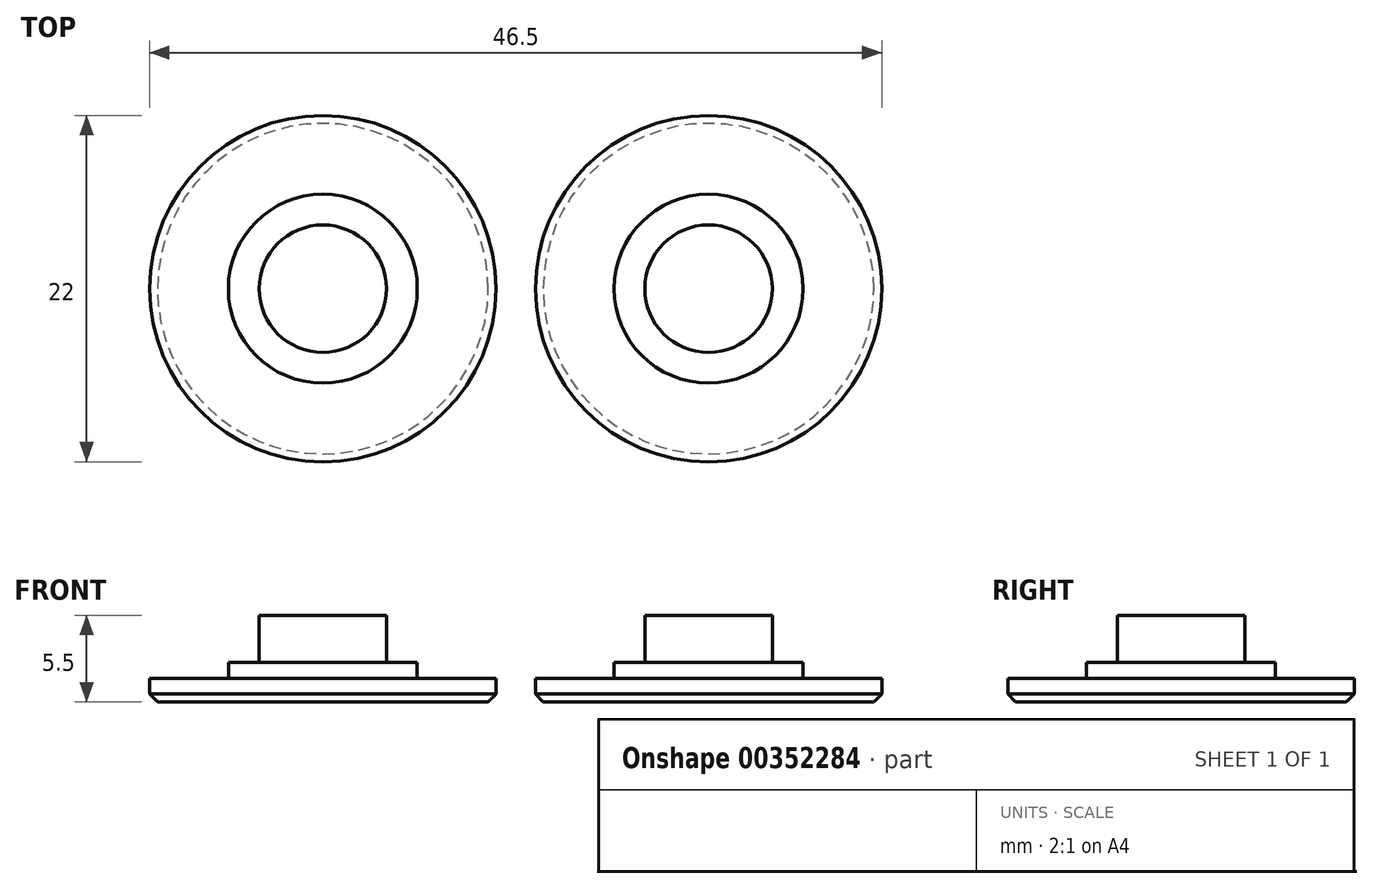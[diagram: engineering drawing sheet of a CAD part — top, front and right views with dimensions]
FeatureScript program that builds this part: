
annotation { "Feature Type Name" : "Feature", "Feature Type Description" : "" }
export const myFeature = defineFeature(function(context is Context, id is Id, definition is map)
    precondition{}
    {
        {
            var Q0;
            Q0=qCreatedBy(makeId("Top.planeOp"),FACE);
            var sketch = newSketch(context, id + "F0", { "sketchPlane" : qUnion([Q0])});
            skCircle(sketch, "E0", {"center": v(0, 0) * mm, "radius": 11 * mm});
            skSolve(sketch);
        }
        {
            var Q0;
            Q0 = qSketchRegion(id + "F0", true);
            extrude(context, id + "F1", {"entities" : qUnion([Q0]), "depth" : 1.5 * mm});
        }
        {
            var Q0;
            Q0=makeQuery(id+"F1.opExtrude","CAP_FACE",FACE,{"disambiguationData":[OSD([sQuery(id+"F0.wireOp",EDGE,"E0")])],"isStart":false});
            var sketch = newSketch(context, id + "F2", { "sketchPlane" : qUnion([Q0])});
            skCircle(sketch, "E1", {"center": v(0, 0) * mm, "radius": 6 * mm});
            skSolve(sketch);
        }
        {
            var Q0;
            Q0=makeQuery(id+"F2.imprint","IMPRINT",FACE,{"disambiguationData":[TD([[makeQuery(id+"F2.imprint","IMPRINT",EDGE,{"derivedFrom":sQuery(id+"F2.wireOp",EDGE,"E1")}),1.0]])]});
            extrude(context, id + "F3", {"entities" : qUnion([Q0]), "operationType" : NewBodyOperationType.ADD, "depth" : 1 * mm});
        }
        {
            var Q0;
            Q0=makeQuery(id+"F1.opExtrude","CAP_FACE",FACE,{"disambiguationData":[OSD([sQuery(id+"F0.wireOp",EDGE,"E0")])],"isStart":true});
            chamfer(context, id + "F4", {"entities" : qUnion([Q0]), "width" : .5 * mm, "tangentPropagation" : true});
        }
        {
            var Q0;
            Q0=makeQuery(id+"F3.opExtrude","CAP_FACE",FACE,{"disambiguationData":[OSD([sQuery(id+"F2.wireOp",EDGE,"E1")])],"isStart":false});
            var sketch = newSketch(context, id + "F5", { "sketchPlane" : qUnion([Q0])});
            skCircle(sketch, "E2", {"center": v(0, 0) * mm, "radius": 4.05 * mm});
            skSolve(sketch);
        }
        {
            var Q0;
            Q0=makeQuery(id+"F5.imprint","IMPRINT",FACE,{"disambiguationData":[TD([[makeQuery(id+"F5.imprint","IMPRINT",EDGE,{"derivedFrom":sQuery(id+"F5.wireOp",EDGE,"E2")}),1.0]])]});
            extrude(context, id + "F6", {"entities" : qUnion([Q0]), "operationType" : NewBodyOperationType.ADD, "depth" : 3 * mm});
        }
        {
            var Q0;
            Q0=makeQuery(id+"F1.opExtrude","SWEPT_BODY",BODY,{"disambiguationData":[OSD([sQuery(id+"F0.wireOp",EDGE,"E0")])]});
            transform(context, id + "F7", {"entities" : qUnion([Q0]), "transformType" : TransformType.TRANSLATION_3D, "dx" : 24.5 * mm, "dy" : 0 * mm, "dz" : 0 * mm, "makeCopy" : true});
        }
    });
